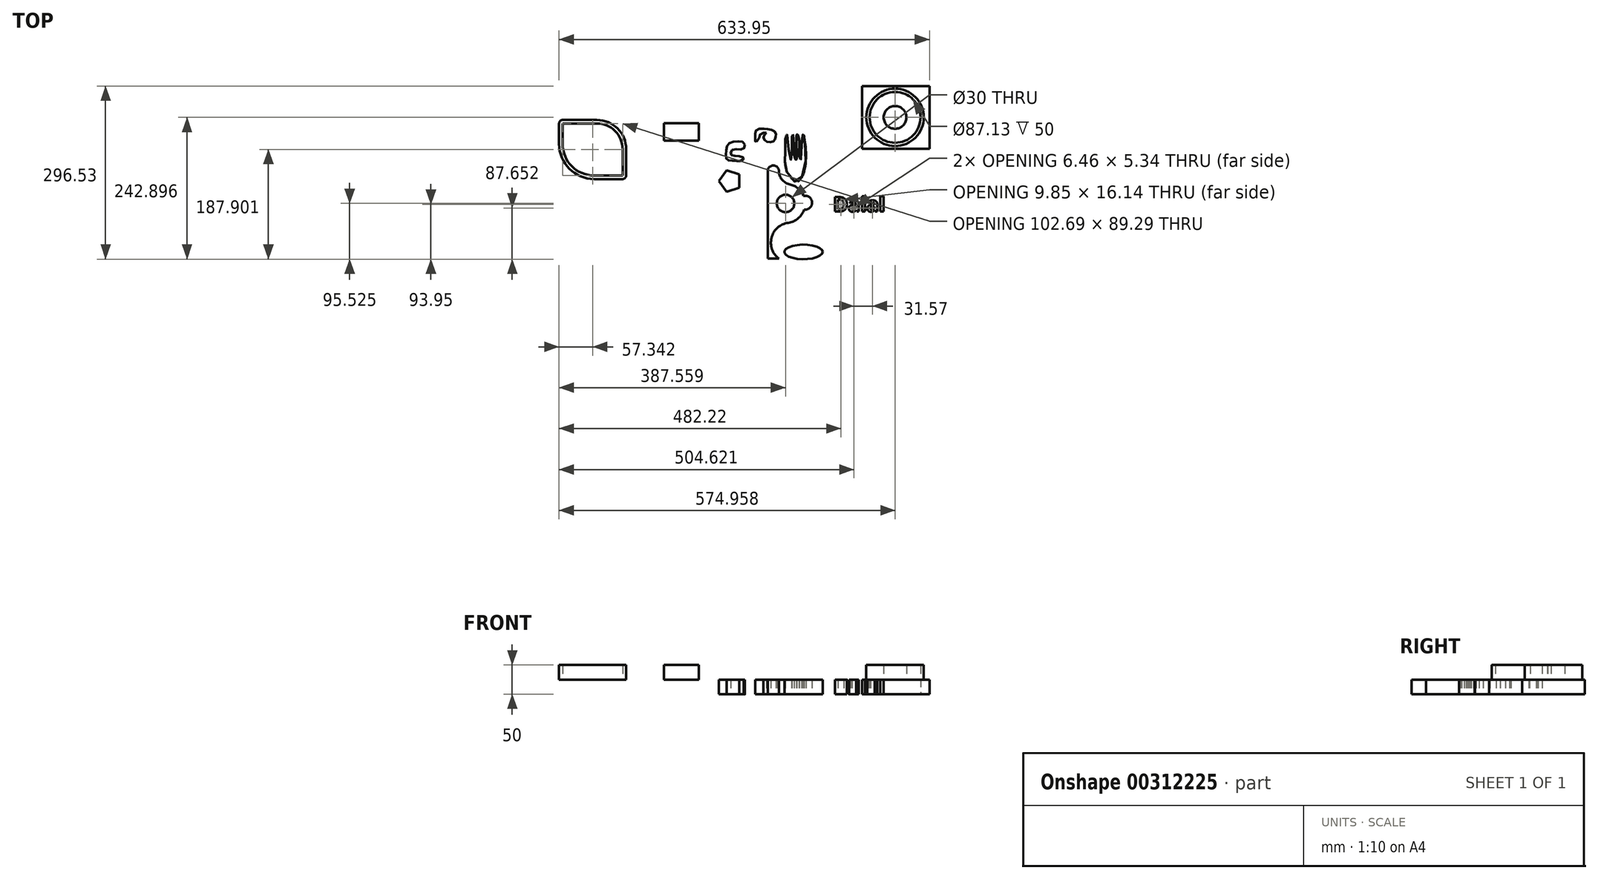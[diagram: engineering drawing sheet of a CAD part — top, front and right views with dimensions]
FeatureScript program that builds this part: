
annotation { "Feature Type Name" : "Feature", "Feature Type Description" : "" }
export const myFeature = defineFeature(function(context is Context, id is Id, definition is map)
    precondition{}
    {
        {
            var Q0;
            Q0=qCreatedBy(makeId("Top.planeOp"),FACE);
            var sketch = newSketch(context, id + "F0", { "sketchPlane" : qUnion([Q0])});
            skLineSegment(sketch, "E0.bottom", {"start": v(113.17, 2.33) * mm, "end": v(93.97, 2.33) * mm});
            skLineSegment(sketch, "E0.right", {"start": v(93.97, 2.33) * mm, "end": v(93.97, 152.33) * mm});
            skPoint(sketch, "E0.middle", {"position": v(103.57, 77.33) * mm});
            skEllipse(sketch, "E1", {"center": v(155.38, 13.9) * mm, "majorRadius": 32.7 * mm, "minorRadius": 12.5 * mm, "majorAxis": v(1, 0)});
            skArc(sketch, "E2", {"start": v(93.97, 152.33) * mm, "mid": v(103.57, 161.93) * mm, "end": v(113.17, 152.33) * mm});
            skArc(sketch, "E3", {"start": v(113.17, 152.33) * mm, "mid": v(118.32, 137.76) * mm, "end": v(131.5, 129.66) * mm});
            skArc(sketch, "E4", {"start": v(131.5, 129.66) * mm, "mid": v(157.93, 95.67) * mm, "end": v(129.01, 63.76) * mm});
            skArc(sketch, "E5", {"start": v(129.01, 63.76) * mm, "mid": v(100.47, 38.36) * mm, "end": v(113.17, 2.33) * mm});
            skCircle(sketch, "E6", {"center": v(124.48, 96.93) * mm, "radius": 15 * mm});
            skCircle(sketch, "E7", {"center": v(124.48, 96.93) * mm, "radius": 7.5 * mm});
            skCircle(sketch, "E8.cCircle", {"center": v(29.52, 135.16) * mm, "radius": 15.55 * mm, "construction": true});
            skLineSegment(sketch, "E8.0", {"start": v(45.07, 146.46) * mm, "end": v(45.07, 123.86) * mm});
            skLineSegment(sketch, "E8.1", {"start": v(45.07, 123.86) * mm, "end": v(23.58, 116.88) * mm});
            skLineSegment(sketch, "E8.2", {"start": v(23.58, 116.88) * mm, "end": v(10.3, 135.16) * mm});
            skLineSegment(sketch, "E8.3", {"start": v(10.3, 135.16) * mm, "end": v(23.58, 153.44) * mm});
            skLineSegment(sketch, "E8.4", {"start": v(23.58, 153.44) * mm, "end": v(45.07, 146.46) * mm});
            skPoint(sketch, "E8.0.midPoint", {"position": v(45.07, 135.16) * mm});
            skFitSpline(sketch, "E9", {"points": [v(45.1, 177.83) * mm, v(32.58, 179.33) * mm, v(30.58, 185.34) * mm, v(38.6, 189.85) * mm, v(53.12, 190.85) * mm, v(53.12, 200.87) * mm, v(39.1, 202.87) * mm, v(25.57, 197.86) * mm, v(22.56, 183.34) * mm, v(23.57, 172.32) * mm, v(34.58, 169.82) * mm, v(47.6, 169.82) * mm, v(53.12, 173.82) * mm, v(45.1, 177.83) * mm]});
            skFitSpline(sketch, "E10", {"points": [v(91.68, 217.9) * mm, v(87.17, 213.4) * mm, v(88.18, 205.88) * mm, v(93.19, 202.37) * mm, v(102.2, 202.37) * mm, v(105.7, 205.88) * mm, v(107.71, 211.89) * mm, v(107.2, 218.9) * mm, v(99.2, 222.9) * mm, v(87.17, 224.91) * mm, v(73.65, 221.9) * mm, v(72.65, 210.89) * mm, v(73.15, 202.37) * mm, v(79.66, 209.38) * mm, v(81.67, 215.9) * mm, v(91.68, 217.9) * mm]});
            skFitSpline(sketch, "E11", {"points": [v(124.24, 186.85) * mm, v(123.85, 208.9) * mm, v(126.22, 216.1) * mm, v(128.2, 209.23) * mm, v(131.75, 176.33) * mm, v(133.86, 171.51) * mm, v(135.23, 176.35) * mm, v(134.8, 209.62) * mm, v(136.7, 215.1) * mm, v(137.76, 209.89) * mm, v(139.77, 176.83) * mm, v(142.27, 171.32) * mm, v(143.77, 177.33) * mm, v(142.77, 209.38) * mm, v(144.27, 215.4) * mm, v(147.28, 208.88) * mm, v(147.78, 177.33) * mm, v(149.28, 170.32) * mm, v(151.79, 176.33) * mm, v(152.29, 208.38) * mm, v(154.3, 214.9) * mm, v(156.8, 207.88) * mm, v(158.3, 162.8) * mm, v(147.28, 135.76) * mm, v(138.26, 135.26) * mm, v(124.56, 155.65) * mm, v(123.43, 169.13) * mm, v(124.24, 186.85) * mm]});
            skPoint(sketch, "E12", {"position": v(157.93, 98.19) * mm});
            skPoint(sketch, "E12.positionSnap0", {"position": v(157.93, 95.67) * mm});
            skPoint(sketch, "E13", {"position": v(156.14, 107.8) * mm});
            skCircle(sketch, "E14", {"center": v(157.93, 98.19) * mm, "radius": 11.9 * mm});
            skText(sketch, "E15", { "text": "Dalal", "fontName": "OpenSans-Bold.ttf"});
            skLineSegment(sketch, "E16.bottom", {"start": v(255.18, 297.93) * mm, "end": v(370.87, 297.93) * mm});
            skLineSegment(sketch, "E16.top", {"start": v(255.18, 190.66) * mm, "end": v(370.87, 190.66) * mm});
            skLineSegment(sketch, "E16.left", {"start": v(255.18, 297.93) * mm, "end": v(255.18, 190.66) * mm});
            skLineSegment(sketch, "E16.right", {"start": v(370.87, 297.93) * mm, "end": v(370.87, 190.66) * mm});
            skCircle(sketch, "E17", {"center": v(311.88, 244.3) * mm, "radius": 43.56 * mm});
            skPoint(sketch, "E17.centerSnap0", {"position": v(255.18, 244.3) * mm});
            const initialGuessF0  = {"E15": [0.20584, 0.08294, 1, 0, 0.025]};
            skSetInitialGuess(sketch, initialGuessF0);
            skSolve(sketch);
        }
        {
            var Q0;
            Q0 = qSketchRegion(id + "F0", true);
            extrude(context, id + "F1", {"entities" : qUnion([Q0]), "depth" : 25 * mm});
        }
        {
            var Q0;
            Q0=makeQuery(id+"F1.opExtrude","CAP_FACE",FACE,{"disambiguationData":[OSD([sQuery(id+"F0.wireOp",EDGE,"E16.bottom"),sQuery(id+"F0.wireOp",EDGE,"E16.top"),sQuery(id+"F0.wireOp",EDGE,"E16.left"),sQuery(id+"F0.wireOp",EDGE,"E16.right"),sQuery(id+"F0.wireOp",EDGE,"E17")])],"isStart":false});
            var sketch = newSketch(context, id + "F2", { "sketchPlane" : qUnion([Q0])});
            skCircle(sketch, "E18.0", {"center": v(311.88, 244.3) * mm, "radius": 43.56 * mm});
            skCircle(sketch, "E19", {"center": v(311.88, 244.3) * mm, "radius": 19.48 * mm});
            skCircle(sketch, "E20.0", {"center": v(311.88, 244.3) * mm, "radius": 49.16 * mm});
            skLineSegment(sketch, "E21.bottom", {"start": v(-257.08, 239.95) * mm, "end": v(-198.4, 239.95) * mm});
            skLineSegment(sketch, "E21.top", {"start": v(-203.08, 138.66) * mm, "end": v(-154.4, 138.66) * mm});
            skLineSegment(sketch, "E21.left", {"start": v(-263.08, 233.95) * mm, "end": v(-263.08, 198.66) * mm});
            skLineSegment(sketch, "E21.right", {"start": v(-148.4, 189.95) * mm, "end": v(-148.4, 144.66) * mm});
            skPoint(sketch, "E22.visualSharp", {"position": v(-263.08, 239.95) * mm});
            skArc(sketch, "E22.filletArc", {"start": v(-257.08, 239.95) * mm, "mid": v(-261.33, 238.19) * mm, "end": v(-263.08, 233.95) * mm});
            skPoint(sketch, "E23.visualSharp", {"position": v(-148.4, 239.95) * mm});
            skArc(sketch, "E23.filletArc", {"start": v(-148.4, 189.95) * mm, "mid": v(-163.04, 225.3) * mm, "end": v(-198.4, 239.95) * mm});
            skPoint(sketch, "E24.visualSharp", {"position": v(-148.4, 138.66) * mm});
            skArc(sketch, "E24.filletArc", {"start": v(-154.4, 138.66) * mm, "mid": v(-150.15, 140.41) * mm, "end": v(-148.4, 144.66) * mm});
            skPoint(sketch, "E25.visualSharp", {"position": v(-263.08, 138.66) * mm});
            skArc(sketch, "E25.filletArc", {"start": v(-263.08, 198.66) * mm, "mid": v(-245.5, 156.23) * mm, "end": v(-203.08, 138.66) * mm});
            skLineSegment(sketch, "E26.0", {"start": v(-257.08, 233.95) * mm, "end": v(-257.08, 198.66) * mm});
            skArc(sketch, "E26.1", {"start": v(-154.4, 189.95) * mm, "mid": v(-167.28, 221.06) * mm, "end": v(-198.4, 233.95) * mm});
            skLineSegment(sketch, "E26.2", {"start": v(-154.4, 189.95) * mm, "end": v(-154.4, 144.66) * mm});
            skLineSegment(sketch, "E26.3", {"start": v(-257.08, 233.95) * mm, "end": v(-198.4, 233.95) * mm});
            skLineSegment(sketch, "E26.4", {"start": v(-203.08, 144.66) * mm, "end": v(-154.4, 144.66) * mm});
            skArc(sketch, "E26.5", {"start": v(-257.08, 198.66) * mm, "mid": v(-241.27, 160.47) * mm, "end": v(-203.08, 144.66) * mm});
            skLineSegment(sketch, "E27.bottom", {"start": v(-83.74, 234.29) * mm, "end": v(-23.74, 234.29) * mm});
            skLineSegment(sketch, "E27.top", {"start": v(-83.74, 204.29) * mm, "end": v(-23.74, 204.29) * mm});
            skLineSegment(sketch, "E27.left", {"start": v(-83.74, 234.29) * mm, "end": v(-83.74, 204.29) * mm});
            skLineSegment(sketch, "E27.right", {"start": v(-23.74, 234.29) * mm, "end": v(-23.74, 204.29) * mm});
            skSolve(sketch);
        }
        {
            var Q0;
            Q0 = qSketchRegion(id + "F2", true);
            var Q1;
            Q1=makeQuery(id+"F2.imprint","IMPRINT",FACE,{"disambiguationData":[TD([[makeQuery(id+"F2.imprint","IMPRINT",EDGE,{"derivedFrom":sQuery(id+"F2.wireOp",EDGE,"E19")}),1.0]])]});
            extrude(context, id + "F3", {"entities" : qUnion([Q0, Q1]), "operationType" : NewBodyOperationType.ADD, "depth" : 25 * mm});
        }
    });
